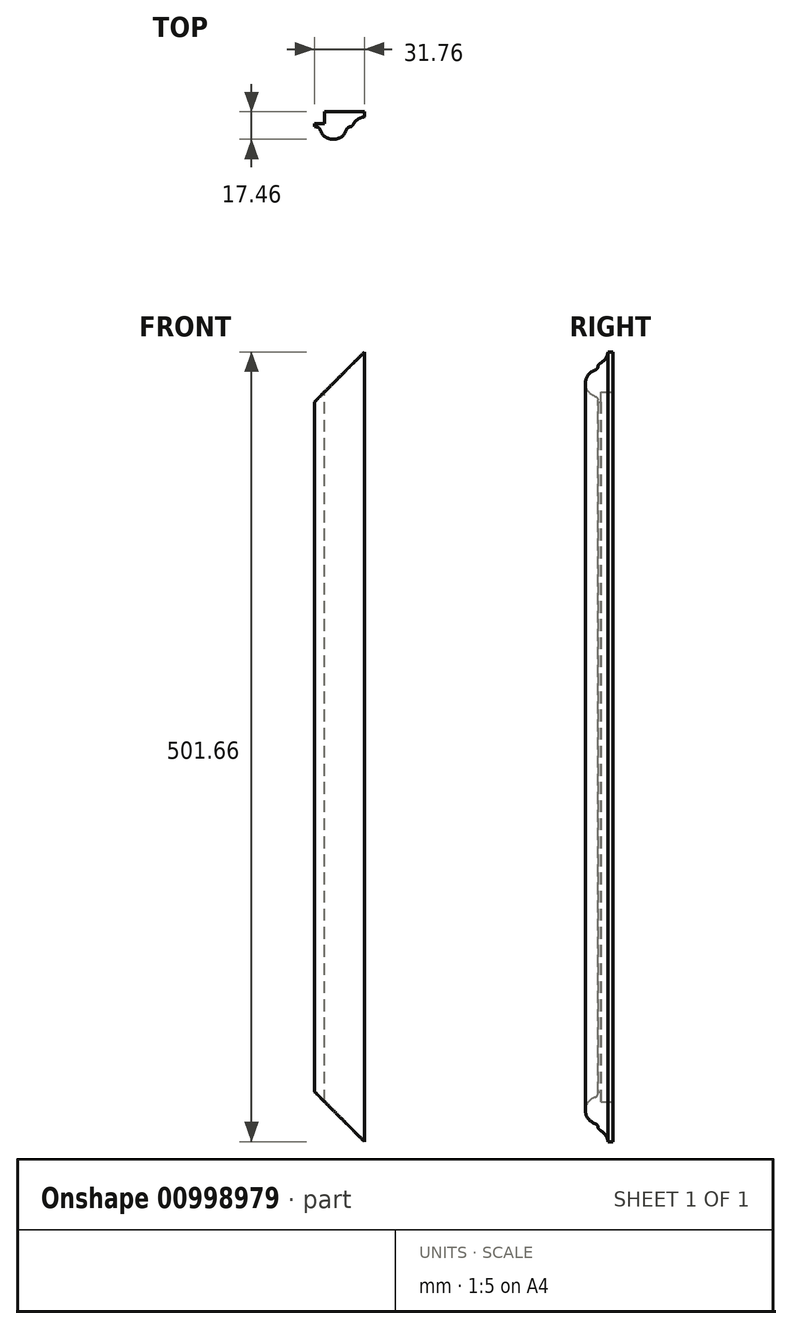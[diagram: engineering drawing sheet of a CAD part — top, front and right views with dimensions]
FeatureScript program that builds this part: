
annotation { "Feature Type Name" : "Feature", "Feature Type Description" : "" }
export const myFeature = defineFeature(function(context is Context, id is Id, definition is map)
    precondition{}
    {
        {
            var Q0;
            Q0=qCreatedBy(makeId("Top.planeOp"),FACE);
            var sketch = newSketch(context, id + "F0", { "sketchPlane" : qUnion([Q0])});
            skLineSegment(sketch, "E0.bottom", {"start": v(15.88, 8.73) * mm, "end": v(-15.88, 8.73) * mm});
            skLineSegment(sketch, "E0.top", {"start": v(-3.97, -8.73) * mm, "end": v(-3.98, -8.73) * mm});
            skLineSegment(sketch, "E0.left", {"start": v(15.88, 8.73) * mm, "end": v(15.88, -0.8) * mm});
            skLineSegment(sketch, "E0.right", {"start": v(-15.88, 8.73) * mm, "end": v(-15.88, -0.8) * mm});
            skPoint(sketch, "E0.middle", {"position": v(0, 0) * mm});
            skLineSegment(sketch, "E1", {"start": v(15.88, 8.73) * mm, "end": v(15.88, 5.56) * mm});
            skLineSegment(sketch, "E2", {"start": v(-19.4, -0.8) * mm, "end": v(24.15, -0.8) * mm, "construction": true});
            skLineSegment(sketch, "E3", {"start": v(21.72, 5.56) * mm, "end": v(-20.21, 5.56) * mm, "construction": true});
            skPoint(sketch, "E4", {"position": v(7.94, -0.8) * mm});
            skPoint(sketch, "E5", {"position": v(4.76, -0.8) * mm});
            skPoint(sketch, "E6", {"position": v(-12.7, -0.8) * mm});
            skLineSegment(sketch, "E7", {"start": v(-15.88, -0.8) * mm, "end": v(-12.7, -0.8) * mm});
            skLineSegment(sketch, "E8", {"start": v(4.76, -0.8) * mm, "end": v(7.94, -0.8) * mm});
            skPoint(sketch, "E9", {"position": v(-3.98, -8.73) * mm});
            skArc(sketch, "E10", {"start": v(15.88, 5.56) * mm, "mid": v(10.99, 3.53) * mm, "end": v(7.94, -0.8) * mm});
            skArc(sketch, "E11", {"start": v(-12.7, -0.8) * mm, "mid": v(-3.97, -8.73) * mm, "end": v(4.76, -0.8) * mm});
            skPoint(sketch, "E12.orphan", {"position": v(-15.88, -8.73) * mm});
            skPoint(sketch, "E13.orphan", {"position": v(15.88, -8.73) * mm});
            skSolve(sketch);
        }
        {
            var Q0;
            Q0=makeQuery(id+"F0.imprint","IMPRINT",FACE,{"disambiguationData":[TD([[makeQuery(id+"F0.imprint","IMPRINT",EDGE,{"derivedFrom":sQuery(id+"F0.wireOp",EDGE,"E0.bottom")}),1.0]])]});
            extrude(context, id + "F1", {"entities" : qUnion([Q0]), "endBound" : BoundingType.SYMMETRIC, "depth" : 501.65 * mm, "offsetDistance" : 25.4 * mm});
        }
        {
            var Q0;
            Q0=makeQuery(id+"F1.opExtrude","SWEPT_EDGE",EDGE,{"disambiguationData":[OSD([sQuery(id+"F0.wireOp",EDGE,"E8"),sQuery(id+"F0.wireOp",EDGE,"E10")])]});
            fillet(context, id + "F2", {"entities" : qUnion([Q0]), "radius" : 2.54 * mm, "tangentPropagation" : true, "allowEdgeOverflow" : false});
        }
        {
            var Q0;
            Q0=makeQuery(id+"F1.opExtrude","SWEPT_EDGE",EDGE,{"disambiguationData":[OSD([sQuery(id+"F0.wireOp",EDGE,"E7"),sQuery(id+"F0.wireOp",EDGE,"E11")])]});
            fillet(context, id + "F3", {"entities" : qUnion([Q0]), "radius" : 2.54 * mm, "tangentPropagation" : true, "allowEdgeOverflow" : false});
        }
        {
            var Q0;
            Q0=makeQuery(id+"F1.opExtrude","SWEPT_EDGE",EDGE,{"disambiguationData":[OSD([sQuery(id+"F0.wireOp",EDGE,"E8"),sQuery(id+"F0.wireOp",EDGE,"E11")])]});
            fillet(context, id + "F4", {"entities" : qUnion([Q0]), "radius" : 2.54 * mm, "tangentPropagation" : true, "allowEdgeOverflow" : false});
        }
        {
            var Q0;
            Q0=makeQuery(id+"F1.opExtrude","SWEPT_FACE",FACE,{"disambiguationData":[OSD([sQuery(id+"F0.wireOp",EDGE,"E0.bottom")])]});
            var sketch = newSketch(context, id + "F5", { "sketchPlane" : qUnion([Q0])});
            skLineSegment(sketch, "E14", {"start": v(15.88, -219.07) * mm, "end": v(-15.87, -250.83) * mm});
            skLineSegment(sketch, "E15.MirrorCS", {"start": v(15.88, 219.07) * mm, "end": v(-15.88, 250.83) * mm});
            skLineSegment(sketch, "E16", {"start": v(-15.88, 250.83) * mm, "end": v(15.87, 250.83) * mm});
            skLineSegment(sketch, "E17", {"start": v(15.87, 250.83) * mm, "end": v(15.88, 219.07) * mm});
            skLineSegment(sketch, "E18.MirrorCS", {"start": v(15.88, -250.83) * mm, "end": v(15.88, -219.07) * mm});
            skLineSegment(sketch, "E19.MirrorCS", {"start": v(-15.88, -250.83) * mm, "end": v(15.87, -250.83) * mm});
            skSolve(sketch);
        }
        {
            var Q0;
            Q0=makeQuery(id+"FtKLiYXaFetn44W_1.boolean.opBoolean","SPLIT",FACE,{"disambiguationData":[TD([makeQuery(id+"FtKLiYXaFetn44W_1.opExtrude","SWEPT_FACE",FACE,{"disambiguationData":[OSD([sQuery(id+"FxCuGDugNnE8EV2_1.wireOp",EDGE,"FmI5fHck-0ub2-xswP-vLsR-ZfJuQmsgoC2R")])]})])],"derivedFrom":makeQuery(id+"F1.opExtrude","SWEPT_FACE",FACE,{"disambiguationData":[OSD([sQuery(id+"F0.wireOp",EDGE,"E0.bottom")])]})});
            var sketch = newSketch(context, id + "F6", { "sketchPlane" : qUnion([Q0])});
            skLineSegment(sketch, "E20.bottom", {"start": v(15.88, -250.83) * mm, "end": v(9.52, -250.83) * mm});
            skLineSegment(sketch, "E20.top", {"start": v(15.87, 250.83) * mm, "end": v(9.52, 250.83) * mm});
            skLineSegment(sketch, "E20.left", {"start": v(15.88, -250.83) * mm, "end": v(15.87, 250.83) * mm});
            skLineSegment(sketch, "E20.right", {"start": v(9.52, -250.83) * mm, "end": v(9.52, 250.83) * mm});
            skSolve(sketch);
        }
        {
            var Q0;
            Q0=qSketchRegion(id+"F6",true);
            extrude(context, id + "F7", {"entities" : qUnion([Q0]), "operationType" : NewBodyOperationType.REMOVE, "oppositeDirection" : true, "depth" : 7.62 * mm, "offsetDistance" : 25.4 * mm});
        }
        {
            var Q0;
            Q0=qSketchRegion(id+"F5",true);
            extrude(context, id + "F8", {"entities" : qUnion([Q0]), "operationType" : NewBodyOperationType.REMOVE, "endBound" : BoundingType.THROUGH_ALL, "oppositeDirection" : true, "depth" : 25.4 * mm, "offsetDistance" : 25.4 * mm});
        }
    });
